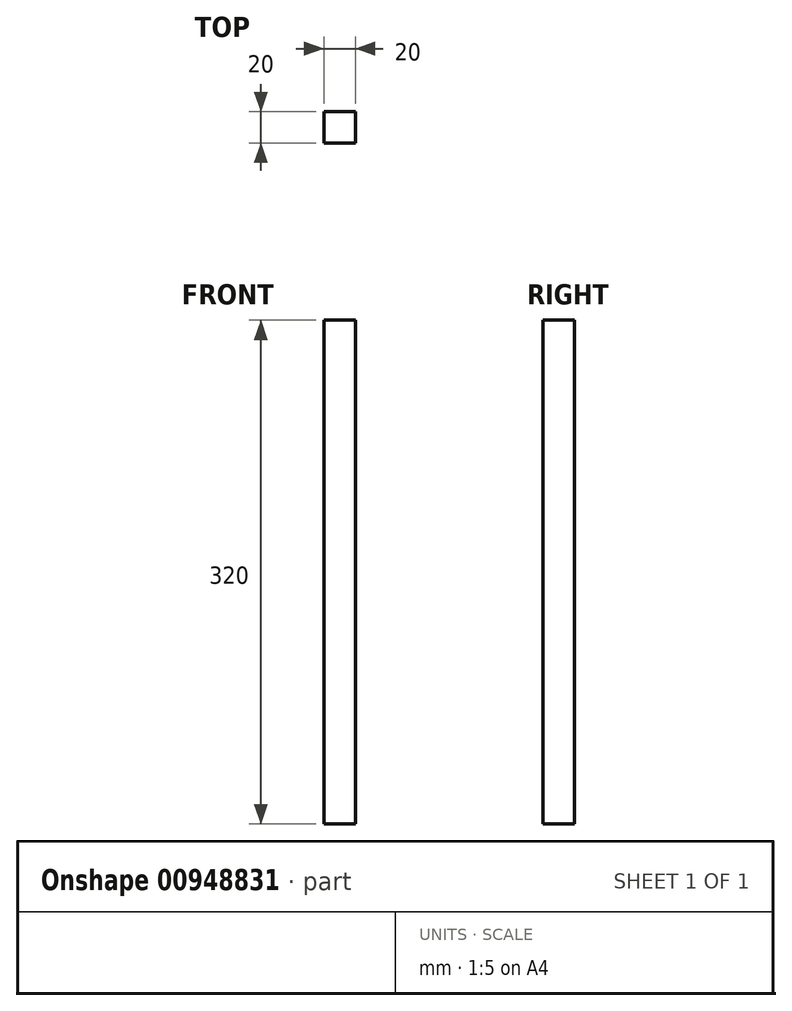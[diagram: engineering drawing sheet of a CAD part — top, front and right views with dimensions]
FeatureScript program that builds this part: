
annotation { "Feature Type Name" : "Feature", "Feature Type Description" : "" }
export const myFeature = defineFeature(function(context is Context, id is Id, definition is map)
    precondition{}
    {
        {
            var Q0;
            Q0=qCreatedBy(makeId("Top.planeOp"),FACE);
            var sketch = newSketch(context, id + "F0", { "sketchPlane" : qUnion([Q0])});
            skLineSegment(sketch, "E0.bottom", {"start": v(10, -10) * mm, "end": v(-10, -10) * mm});
            skLineSegment(sketch, "E0.top", {"start": v(10, 10) * mm, "end": v(-10, 10) * mm});
            skLineSegment(sketch, "E0.left", {"start": v(10, -10) * mm, "end": v(10, 10) * mm});
            skLineSegment(sketch, "E0.right", {"start": v(-10, -10) * mm, "end": v(-10, 10) * mm});
            skPoint(sketch, "E0.middle", {"position": v(0, 0) * mm});
            skSolve(sketch);
        }
        {
            var Q0;
            Q0=qSketchRegion(id+"F0",true);
            extrude(context, id + "F1", {"entities" : qUnion([Q0]), "depth" : 320 * mm, "offsetDistance" : 25 * mm});
        }
    });
